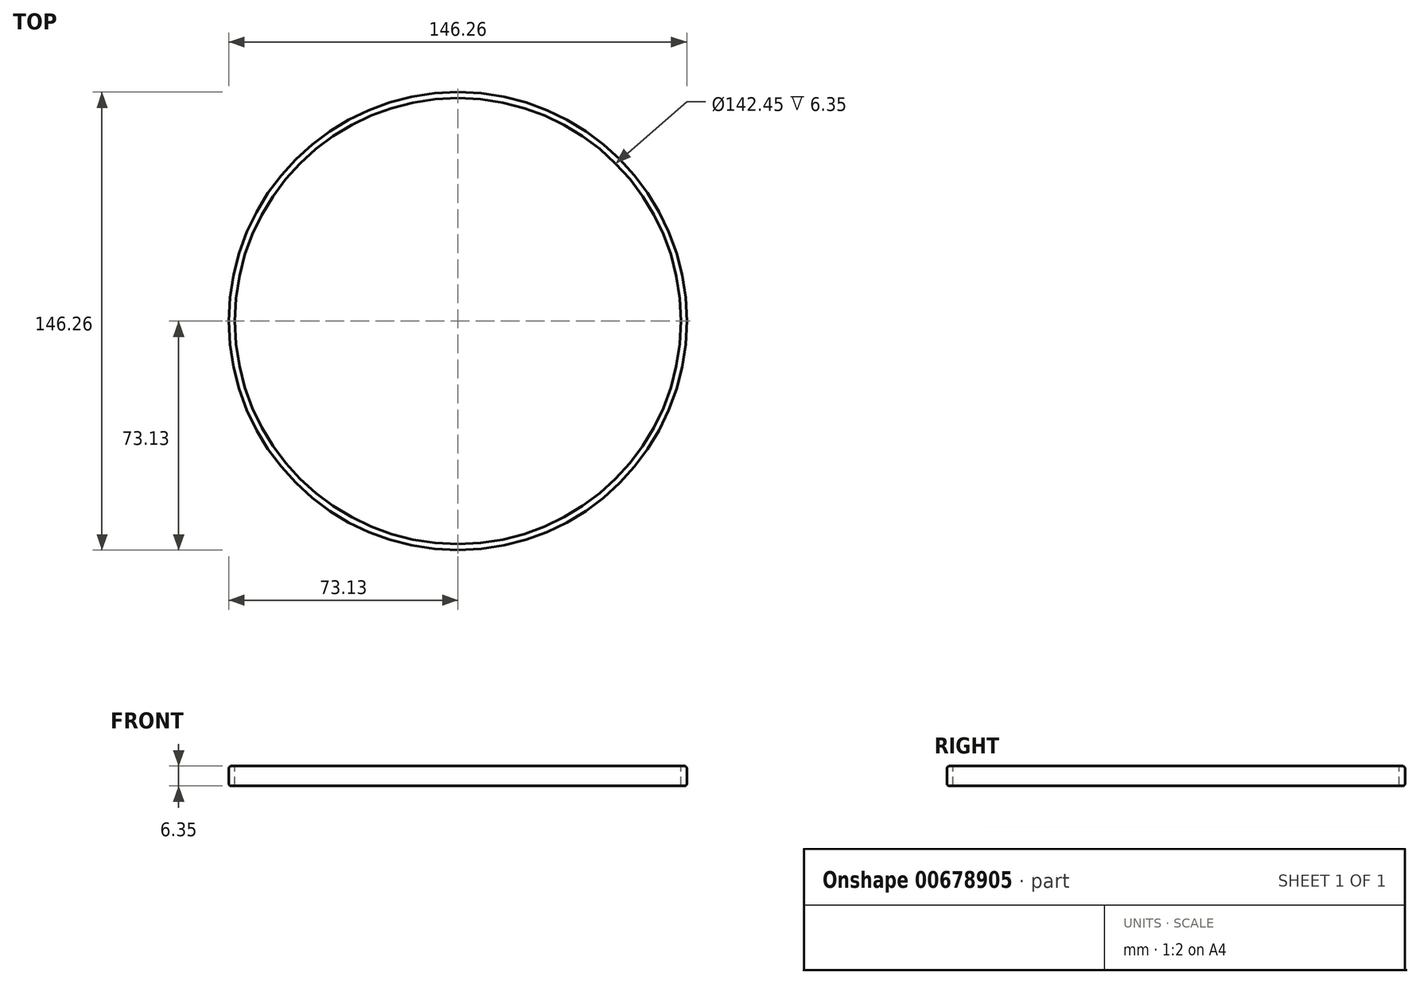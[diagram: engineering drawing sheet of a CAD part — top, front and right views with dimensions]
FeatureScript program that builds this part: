
annotation { "Feature Type Name" : "Feature", "Feature Type Description" : "" }
export const myFeature = defineFeature(function(context is Context, id is Id, definition is map)
    precondition{}
    {
        {
            var Q0;
            Q0=qCreatedBy(makeId("Front.planeOp"),FACE);
            var sketch = newSketch(context, id + "F0", { "sketchPlane" : qUnion([Q0])});
            skLineSegment(sketch, "E0", {"start": v(0, 0) * mm, "end": v(0, -74.93) * mm, "construction": true});
            skLineSegment(sketch, "E1", {"start": v(58.13, -24.81) * mm, "end": v(66.04, -23.7) * mm});
            skLineSegment(sketch, "E2", {"start": v(0, -4.09) * mm, "end": v(71.23, -4.09) * mm});
            skPoint(sketch, "E3.visualSharp", {"position": v(27.87, -75.65) * mm});
            skArc(sketch, "E3.filletArc", {"start": v(18.58, -75.06) * mm, "mid": v(25.06, -73.32) * mm, "end": v(28.19, -67.37) * mm});
            skPoint(sketch, "E4.visualSharp", {"position": v(27.87, -48.38) * mm});
            skArc(sketch, "E4.filletArc", {"start": v(36.42, -49.86) * mm, "mid": v(31.24, -52.35) * mm, "end": v(28.9, -57.6) * mm});
            skPoint(sketch, "E5.visualSharp", {"position": v(50.51, -47.29) * mm});
            skArc(sketch, "E5.filletArc", {"start": v(43.25, -49.17) * mm, "mid": v(48.6, -46.5) * mm, "end": v(50.8, -40.96) * mm});
            skPoint(sketch, "E6.visualSharp", {"position": v(54.25, -25.36) * mm});
            skArc(sketch, "E6.filletArc", {"start": v(58.13, -24.81) * mm, "mid": v(53.01, -27.57) * mm, "end": v(50.92, -32.99) * mm});
            skPoint(sketch, "E7.visualSharp", {"position": v(73.03, -22.7) * mm});
            skArc(sketch, "E7.filletArc", {"start": v(66.04, -23.7) * mm, "mid": v(71.03, -20.97) * mm, "end": v(73.03, -15.64) * mm});
            skArc(sketch, "E8.MirrorCS", {"start": v(-66.04, -23.7) * mm, "mid": v(-71.03, -20.97) * mm, "end": v(-73.03, -15.64) * mm});
            skLineSegment(sketch, "E9.MirrorCS", {"start": v(-58.13, -24.81) * mm, "end": v(-66.04, -23.7) * mm});
            skLineSegment(sketch, "E10.MirrorCS", {"start": v(-43.25, -49.17) * mm, "end": v(-36.42, -49.86) * mm});
            skArc(sketch, "E11.MirrorCS", {"start": v(-43.25, -49.17) * mm, "mid": v(-48.6, -46.5) * mm, "end": v(-50.8, -40.96) * mm});
            skArc(sketch, "E12.MirrorCS", {"start": v(-18.58, -75.06) * mm, "mid": v(-25.06, -73.32) * mm, "end": v(-28.19, -67.37) * mm});
            skArc(sketch, "E13.MirrorCS", {"start": v(-36.42, -49.86) * mm, "mid": v(-31.24, -52.35) * mm, "end": v(-28.9, -57.6) * mm});
            skArc(sketch, "E14.MirrorCS", {"start": v(-58.13, -24.81) * mm, "mid": v(-53.01, -27.57) * mm, "end": v(-50.92, -32.99) * mm});
            skPoint(sketch, "E15.MirrorP", {"position": v(-50.51, -47.29) * mm});
            skLineSegment(sketch, "E16.MirrorCS", {"start": v(-50.92, -32.99) * mm, "end": v(-50.8, -40.96) * mm});
            skPoint(sketch, "E17.MirrorP", {"position": v(-27.87, -48.38) * mm});
            skPoint(sketch, "E18.MirrorP", {"position": v(-27.87, -75.65) * mm});
            skPoint(sketch, "E19.MirrorP", {"position": v(-73.03, -22.7) * mm});
            skLineSegment(sketch, "E20.MirrorCS", {"start": v(0, -4.09) * mm, "end": v(-71.23, -4.09) * mm});
            skPoint(sketch, "E21.MirrorP", {"position": v(-54.25, -25.36) * mm});
            skLineSegment(sketch, "E22", {"start": v(28.9, -57.6) * mm, "end": v(28.19, -67.37) * mm});
            skLineSegment(sketch, "E23.MirrorCS", {"start": v(-28.9, -57.6) * mm, "end": v(-28.19, -67.37) * mm});
            skPoint(sketch, "E24", {"position": v(43.25, -49.17) * mm});
            skLineSegment(sketch, "E25", {"start": v(50.92, -32.99) * mm, "end": v(50.8, -40.96) * mm});
            skLineSegment(sketch, "E26", {"start": v(36.42, -49.86) * mm, "end": v(43.25, -49.17) * mm});
            skArc(sketch, "E27", {"start": v(18.58, -75.06) * mm, "mid": v(9.31, -74) * mm, "end": v(0, -73.66) * mm});
            skArc(sketch, "E28.MirrorCS", {"start": v(-18.58, -75.06) * mm, "mid": v(-9.31, -74) * mm, "end": v(0, -73.66) * mm});
            skLineSegment(sketch, "E29", {"start": v(71.23, -4.09) * mm, "end": v(71.23, -7.26) * mm});
            skLineSegment(sketch, "E30", {"start": v(71.23, -7.26) * mm, "end": v(72.26, -7.26) * mm});
            skLineSegment(sketch, "E31", {"start": v(73.03, -8.02) * mm, "end": v(73.03, -15.64) * mm});
            skPoint(sketch, "E32.visualSharp", {"position": v(73.03, -7.26) * mm});
            skArc(sketch, "E32.filletArc", {"start": v(73.03, -8.02) * mm, "mid": v(72.8, -7.49) * mm, "end": v(72.26, -7.26) * mm});
            skLineSegment(sketch, "E33.MirrorCS", {"start": v(-73.03, -8.02) * mm, "end": v(-73.03, -15.64) * mm});
            skArc(sketch, "E34.MirrorCS", {"start": v(-73.03, -8.02) * mm, "mid": v(-72.8, -7.49) * mm, "end": v(-72.26, -7.26) * mm});
            skLineSegment(sketch, "E35.MirrorCS", {"start": v(-71.23, -7.26) * mm, "end": v(-72.26, -7.26) * mm});
            skLineSegment(sketch, "E36.MirrorCS", {"start": v(-71.23, -4.09) * mm, "end": v(-71.23, -7.26) * mm});
            skPoint(sketch, "E37.orphan", {"position": v(73.03, -4.09) * mm});
            skLineSegment(sketch, "E38.MirrorCS", {"start": v(71.23, -4.09) * mm, "end": v(71.23, -0.92) * mm});
            skLineSegment(sketch, "E39.MirrorCS", {"start": v(71.23, -0.92) * mm, "end": v(72.26, -0.92) * mm});
            skArc(sketch, "E40.MirrorCS", {"start": v(73.03, -0.16) * mm, "mid": v(72.8, -0.7) * mm, "end": v(72.26, -0.92) * mm});
            skLineSegment(sketch, "E41.MirrorCS", {"start": v(-71.23, -0.92) * mm, "end": v(-72.26, -0.92) * mm});
            skArc(sketch, "E42.MirrorCS", {"start": v(-73.03, -0.16) * mm, "mid": v(-72.8, -0.7) * mm, "end": v(-72.26, -0.92) * mm});
            skLineSegment(sketch, "E43.MirrorCS", {"start": v(-71.23, -4.09) * mm, "end": v(-71.23, -0.92) * mm});
            skLineSegment(sketch, "E44.MirrorCS", {"start": v(58.13, 16.63) * mm, "end": v(66.04, 15.51) * mm});
            skPoint(sketch, "E45.MirrorP", {"position": v(-54.25, 17.18) * mm});
            skArc(sketch, "E46.MirrorCS", {"start": v(66.04, 15.51) * mm, "mid": v(71.03, 12.8) * mm, "end": v(73.03, 7.46) * mm});
            skArc(sketch, "E47.MirrorCS", {"start": v(58.13, 16.63) * mm, "mid": v(53.01, 19.39) * mm, "end": v(50.92, 24.8) * mm});
            skLineSegment(sketch, "E48.MirrorCS", {"start": v(73.03, -0.16) * mm, "end": v(73.03, 7.46) * mm});
            skLineSegment(sketch, "E49.MirrorCS", {"start": v(-58.13, 16.63) * mm, "end": v(-66.04, 15.51) * mm});
            skPoint(sketch, "E50.MirrorP", {"position": v(-50.51, 39.1) * mm});
            skArc(sketch, "E51.MirrorCS", {"start": v(-58.13, 16.63) * mm, "mid": v(-53.01, 19.39) * mm, "end": v(-50.92, 24.8) * mm});
            skPoint(sketch, "E52.MirrorP", {"position": v(73.03, -0.92) * mm});
            skPoint(sketch, "E53.MirrorP", {"position": v(27.87, 67.47) * mm});
            skLineSegment(sketch, "E54.MirrorCS", {"start": v(-28.9, 49.42) * mm, "end": v(-28.19, 59.19) * mm});
            skArc(sketch, "E55.MirrorCS", {"start": v(36.42, 41.68) * mm, "mid": v(31.24, 44.17) * mm, "end": v(28.9, 49.42) * mm});
            skArc(sketch, "E56.MirrorCS", {"start": v(-66.04, 15.51) * mm, "mid": v(-71.03, 12.8) * mm, "end": v(-73.03, 7.46) * mm});
            skArc(sketch, "E57.MirrorCS", {"start": v(18.58, 66.88) * mm, "mid": v(25.06, 65.14) * mm, "end": v(28.19, 59.19) * mm});
            skArc(sketch, "E58.MirrorCS", {"start": v(43.25, 41) * mm, "mid": v(48.6, 38.33) * mm, "end": v(50.8, 32.78) * mm});
            skArc(sketch, "E59.MirrorCS", {"start": v(-18.58, 66.88) * mm, "mid": v(-25.06, 65.14) * mm, "end": v(-28.19, 59.19) * mm});
            skArc(sketch, "E60.MirrorCS", {"start": v(-43.25, 41) * mm, "mid": v(-48.6, 38.33) * mm, "end": v(-50.8, 32.78) * mm});
            skArc(sketch, "E61.MirrorCS", {"start": v(18.58, 66.88) * mm, "mid": v(9.31, 65.83) * mm, "end": v(0, 65.48) * mm});
            skLineSegment(sketch, "E62.MirrorCS", {"start": v(-50.92, 24.8) * mm, "end": v(-50.8, 32.78) * mm});
            skPoint(sketch, "E63.MirrorP", {"position": v(43.25, 41) * mm});
            skPoint(sketch, "E64.MirrorP", {"position": v(-27.87, 67.47) * mm});
            skPoint(sketch, "E65.MirrorP", {"position": v(27.87, 40.2) * mm});
            skPoint(sketch, "E66.MirrorP", {"position": v(-27.87, 40.2) * mm});
            skPoint(sketch, "E67.MirrorP", {"position": v(-73.03, 14.52) * mm});
            skLineSegment(sketch, "E68.MirrorCS", {"start": v(50.92, 24.8) * mm, "end": v(50.8, 32.78) * mm});
            skLineSegment(sketch, "E69.MirrorCS", {"start": v(-73.03, -0.16) * mm, "end": v(-73.03, 7.46) * mm});
            skLineSegment(sketch, "E70.MirrorCS", {"start": v(0, -8.18) * mm, "end": v(0, 66.75) * mm, "construction": true});
            skPoint(sketch, "E71.MirrorP", {"position": v(50.51, 39.1) * mm});
            skPoint(sketch, "E72.MirrorP", {"position": v(54.25, 17.18) * mm});
            skArc(sketch, "E73.MirrorCS", {"start": v(-18.58, 66.88) * mm, "mid": v(-9.31, 65.83) * mm, "end": v(0, 65.48) * mm});
            skLineSegment(sketch, "E74.MirrorCS", {"start": v(28.9, 49.42) * mm, "end": v(28.19, 59.19) * mm});
            skPoint(sketch, "E75.MirrorP", {"position": v(73.02, 14.52) * mm});
            skLineSegment(sketch, "E76.MirrorCS", {"start": v(-43.25, 41) * mm, "end": v(-36.42, 41.68) * mm});
            skLineSegment(sketch, "E77.MirrorCS", {"start": v(36.42, 41.68) * mm, "end": v(43.25, 41) * mm});
            skArc(sketch, "E78.MirrorCS", {"start": v(-36.42, 41.68) * mm, "mid": v(-31.24, 44.17) * mm, "end": v(-28.9, 49.42) * mm});
            skLineSegment(sketch, "E79", {"start": v(0, 52.08) * mm, "end": v(0, 0) * mm});
            skSolve(sketch);
        }
        {
            var Q0;
            Q0=sQuery(id+"F0.wireOp",EDGE,"E30");
            var Q1;
            Q1=sQuery(id+"F0.wireOp",EDGE,"E32.filletArc");
            var Q2;
            Q2=sQuery(id+"F0.wireOp",EDGE,"E31");
            var Q3;
            Q3=sQuery(id+"F0.wireOp",EDGE,"E7.filletArc");
            var Q4;
            Q4=sQuery(id+"F0.wireOp",EDGE,"E1");
            var Q5;
            Q5=sQuery(id+"F0.wireOp",EDGE,"E6.filletArc");
            var Q6;
            Q6=sQuery(id+"F0.wireOp",EDGE,"E25");
            var Q7;
            Q7=sQuery(id+"F0.wireOp",EDGE,"E5.filletArc");
            var Q8;
            Q8=sQuery(id+"F0.wireOp",EDGE,"E26");
            var Q9;
            Q9=sQuery(id+"F0.wireOp",EDGE,"E4.filletArc");
            var Q10;
            Q10=sQuery(id+"F0.wireOp",EDGE,"E22");
            var Q11;
            Q11=sQuery(id+"F0.wireOp",EDGE,"E3.filletArc");
            var Q12;
            Q12=sQuery(id+"F0.wireOp",EDGE,"E27");
            var Q13;
            Q13=sQuery(id+"F0.wireOp",EDGE,"E29");
            var Q14;
            Q14=sQuery(id+"F0.wireOp",EDGE,"E0");
            revolve(context, id + "F1", {"bodyType" : ToolBodyType.SURFACE, "surfaceOperationType" : NewSurfaceOperationType.NEW, "surfaceEntities" : qUnion([Q0, Q1, Q2, Q3, Q4, Q5, Q6, Q7, Q8, Q9, Q10, Q11, Q12, Q13]), "axis" : qUnion([Q14]), "revolveType" : RevolveType.FULL});
        }
        {
            var Q0;
            Q0=qCreatedBy(makeId("Front.planeOp"),FACE);
            var sketch = newSketch(context, id + "F2", { "sketchPlane" : qUnion([Q0])});
            skLineSegment(sketch, "E80.bottom", {"start": v(71.23, -7.26) * mm, "end": v(72.37, -7.26) * mm});
            skLineSegment(sketch, "E80.top", {"start": v(71.23, -0.91) * mm, "end": v(72.37, -0.91) * mm});
            skLineSegment(sketch, "E80.left", {"start": v(71.23, -7.26) * mm, "end": v(71.23, -0.91) * mm});
            skLineSegment(sketch, "E80.right", {"start": v(73.13, -6.5) * mm, "end": v(73.13, -1.68) * mm});
            skPoint(sketch, "E81.visualSharp", {"position": v(73.13, -0.91) * mm});
            skArc(sketch, "E81.filletArc", {"start": v(73.13, -1.68) * mm, "mid": v(72.9, -1.14) * mm, "end": v(72.37, -0.91) * mm});
            skPoint(sketch, "E82.visualSharp", {"position": v(73.13, -7.26) * mm});
            skArc(sketch, "E82.filletArc", {"start": v(72.37, -7.26) * mm, "mid": v(72.9, -7.04) * mm, "end": v(73.13, -6.5) * mm});
            skPoint(sketch, "E83.0", {"position": v(71.23, -4.09) * mm});
            skSolve(sketch);
        }
        {
            var Q0;
            Q0=qSketchRegion(id+"F2",true);
            var Q1;
            Q1=sQuery(id+"F0.wireOp",EDGE,"E0");
            revolve(context, id + "F3", {"surfaceOperationType" : NewSurfaceOperationType.NEW, "entities" : qUnion([Q0]), "axis" : qUnion([Q1]), "revolveType" : RevolveType.FULL});
        }
        {
            var Q0;
            Q0=sQuery(id+"F0.wireOp",EDGE,"E61.MirrorCS");
            var Q1;
            Q1=sQuery(id+"F0.wireOp",EDGE,"E57.MirrorCS");
            var Q2;
            Q2=sQuery(id+"F0.wireOp",EDGE,"E74.MirrorCS");
            var Q3;
            Q3=sQuery(id+"F0.wireOp",EDGE,"E55.MirrorCS");
            var Q4;
            Q4=sQuery(id+"F0.wireOp",EDGE,"E77.MirrorCS");
            var Q5;
            Q5=sQuery(id+"F0.wireOp",EDGE,"E58.MirrorCS");
            var Q6;
            Q6=sQuery(id+"F0.wireOp",EDGE,"E68.MirrorCS");
            var Q7;
            Q7=sQuery(id+"F0.wireOp",EDGE,"E47.MirrorCS");
            var Q8;
            Q8=sQuery(id+"F0.wireOp",EDGE,"E44.MirrorCS");
            var Q9;
            Q9=sQuery(id+"F0.wireOp",EDGE,"E46.MirrorCS");
            var Q10;
            Q10=sQuery(id+"F0.wireOp",EDGE,"E48.MirrorCS");
            var Q11;
            Q11=sQuery(id+"F0.wireOp",EDGE,"E40.MirrorCS");
            var Q12;
            Q12=sQuery(id+"F0.wireOp",EDGE,"E38.MirrorCS");
            var Q13;
            Q13=sQuery(id+"F0.wireOp",EDGE,"E39.MirrorCS");
            var Q14;
            Q14=sQuery(id+"F0.wireOp",EDGE,"E70.MirrorCS");
            revolve(context, id + "F4", {"bodyType" : ToolBodyType.SURFACE, "surfaceOperationType" : NewSurfaceOperationType.NEW, "surfaceEntities" : qUnion([Q0, Q1, Q2, Q3, Q4, Q5, Q6, Q7, Q8, Q9, Q10, Q11, Q12, Q13]), "axis" : qUnion([Q14]), "revolveType" : RevolveType.FULL});
        }
    });
